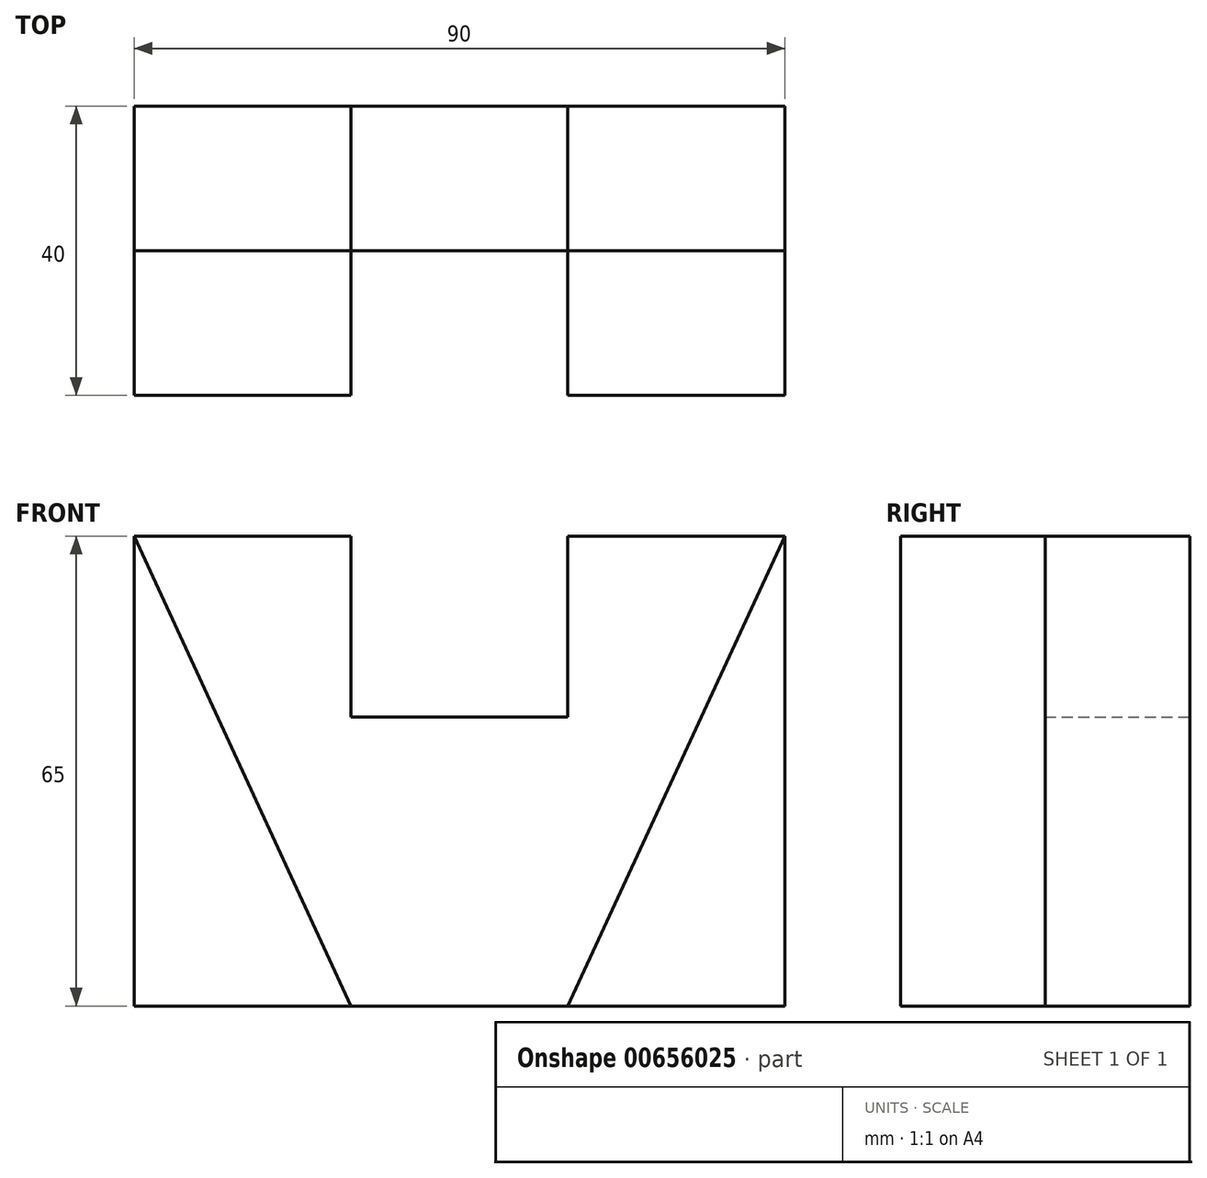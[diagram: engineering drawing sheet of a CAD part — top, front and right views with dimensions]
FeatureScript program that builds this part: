
annotation { "Feature Type Name" : "Feature", "Feature Type Description" : "" }
export const myFeature = defineFeature(function(context is Context, id is Id, definition is map)
    precondition{}
    {
        {
            var Q0;
            Q0=qCreatedBy(makeId("Front.planeOp"),FACE);
            var sketch = newSketch(context, id + "F0", { "sketchPlane" : qUnion([Q0])});
            skLineSegment(sketch, "E0.bottom", {"start": v(45, 32.5) * mm, "end": v(15, 32.5) * mm});
            skLineSegment(sketch, "E0.top", {"start": v(45, -32.5) * mm, "end": v(-45, -32.5) * mm});
            skLineSegment(sketch, "E0.left", {"start": v(45, 32.5) * mm, "end": v(45, -32.5) * mm});
            skLineSegment(sketch, "E0.right", {"start": v(-45, 32.5) * mm, "end": v(-45, -32.5) * mm});
            skPoint(sketch, "E0.middle", {"position": v(0, 0) * mm});
            skLineSegment(sketch, "E1", {"start": v(-45, 32.5) * mm, "end": v(-15, 32.5) * mm});
            skLineSegment(sketch, "E2", {"start": v(-45, 32.5) * mm, "end": v(-45, 7.5) * mm});
            skLineSegment(sketch, "E3", {"start": v(45, 32.5) * mm, "end": v(45, 7.5) * mm});
            skLineSegment(sketch, "E4.right", {"start": v(-15, 32.5) * mm, "end": v(-15, 7.5) * mm});
            skLineSegment(sketch, "E5.right", {"start": v(15, 32.5) * mm, "end": v(15, 7.5) * mm});
            skLineSegment(sketch, "E6", {"start": v(-15, 7.5) * mm, "end": v(15, 7.5) * mm});
            skLineSegment(sketch, "E7.trimOffspring", {"start": v(-15, 32.5) * mm, "end": v(-45, 32.5) * mm});
            skSolve(sketch);
        }
        {
            var Q0;
            Q0 = qSketchRegion(id + "F0", true);
            extrude(context, id + "F1", {"entities" : qUnion([Q0]), "depth" : 20 * mm, "offsetDistance" : 25 * mm});
        }
        {
            var Q0;
            Q0=makeQuery(id+"F1.opExtrude","CAP_FACE",FACE,{"disambiguationData":[OSD([sQuery(id+"F0.wireOp",EDGE,"E0.top"),sQuery(id+"F0.wireOp",EDGE,"E0.left"),sQuery(id+"F0.wireOp",EDGE,"E0.right"),sQuery(id+"F0.wireOp",EDGE,"E2"),sQuery(id+"F0.wireOp",EDGE,"E4.right"),sQuery(id+"F0.wireOp",EDGE,"E0.bottom"),sQuery(id+"F0.wireOp",EDGE,"E3"),sQuery(id+"F0.wireOp",EDGE,"E5.right"),sQuery(id+"F0.wireOp",EDGE,"E6"),sQuery(id+"F0.wireOp",EDGE,"E7.trimOffspring")])],"isStart":false});
            var sketch = newSketch(context, id + "F2", { "sketchPlane" : qUnion([Q0])});
            skLineSegment(sketch, "E8", {"start": v(-45, 32.5) * mm, "end": v(-15, -32.5) * mm});
            skLineSegment(sketch, "E9", {"start": v(45, 32.5) * mm, "end": v(15, -32.5) * mm});
            skSolve(sketch);
        }
        {
            var Q0;
            {var subQ0=sQuery(id+"F2.wireOp",EDGE,"E8");Q0=makeQuery(id+"F2.imprint","IMPRINT",FACE,{"disambiguationData":[TD([[makeQuery(id+"F2.imprint","IMPRINT",EDGE,{"derivedFrom":subQ0}),-1.0]])]});}
            var Q1;
            {var subQ0=sQuery(id+"F2.wireOp",EDGE,"E9");Q1=makeQuery(id+"F2.imprint","IMPRINT",FACE,{"disambiguationData":[TD([[makeQuery(id+"F2.imprint","IMPRINT",EDGE,{"derivedFrom":subQ0}),1.0]])]});}
            extrude(context, id + "F3", {"entities" : qUnion([Q0, Q1]), "depth" : 20 * mm, "offsetDistance" : 25 * mm});
        }
    });
